# Revit family: 879-000X1X-001-DN65-600
name_source: partatom
category: Pipe Accessories
units: mm (PartAtom-declared; Revit-internal decimal feet)

## family parameters
Always vertical = Yes
Cut with Voids When Loaded = No
Part Type = Valve - Breaks Into
Round Connector Dimension = Use Diameter
Shared = No
Work Plane-Based = No

## types (39) — shared parameters
1 = 1 mm  [stored 0.00328084 ft]
879-0065-00-14400051199 = DN65_PN10/16
879-0065-00-144000511A0 = DN65_PN10/16
879-0080-00-14400051199 = DN80_PN10/16
879-0080-00-144000511A0 = DN80_PN10/16
879-0100-00-14400051199 = DN100_PN10/16
879-0100-00-144000511A0 = DN100_PN10/16
879-0125-00-14400051199 = DN125_PN10/16
879-0125-00-144000511A0 = DN125_PN10/16
879-0150-00-14400051199 = DN150_PN10/16
879-0150-00-144000511A0 = DN150_PN10/16
879-0200-00-04400051199 = DN200_PN10
879-0200-00-044000511A0 = DN200_PN10
879-0200-00-14400051199 = DN200_PN16
879-0200-00-144000511A0 = DN200_PN16
879-0250-00-144000511A0 = DN250_PN10
879-0300-00-04400051199 = DN300_PN10
879-0300-00-044000511A0 = DN300_PN10
879-0300-00-14400051199 = DN300_PN16
879-0300-00-144000511A0 = DN300_PN16
879-0350-00-04400051199 = DN350_PN10
879-0350-00-044000511A0 = DN350_PN10
879-0350-00-14400051199 = DN350_PN16
879-0350-00-144000511A0 = DN350_PN16
879-0400-00-04400051199 = DN400_PN10
879-0400-00-044000511A0 = DN400_PN10
879-0400-00-14400051199 = DN400_PN16
879-0400-00-144000511A0 = DN400_PN16
879-0450-00-04400051199 = DN450_PN10
879-0450-00-044000511A0 = DN450_PN10
879-0450-00-14400051199 = DN450_PN16
879-0450-00-144000511A0 = DN450_PN16
879-0500-00-04400051199 = DN500_PN10
879-0500-00-044000511A0 = DN500_PN10
879-0500-00-14400051199 = DN500_PN16
879-0500-00-144000511A0 = DN500_PN16
879-0600-00-04400051199 = DN600_PN10
879-0600-00-044000511A0 = DN600_PN10
879-0600-00-14400051199 = DN600_PN16
879-0600-00-144000511A0 = DN600_PN16
Body_wall_thickness = 10 mm  [stored 0.0328084 ft]
Description_ = AVK PRESSURE REDUCING/PRESSURE SUSTAINING CONTROL VALVE
Search_Table = 879-000X1X-001-DN65-600
URL product pages = https://www.avkvalves.com

## per-type parameters (varying)
- 879-0065-00-14400051199_DN65_PN10/16: Body_Collar_Dia=30 mm  [stored 0.0984252 ft]; Body_Collar_Dia_2=26 mm; Body_Flange_Dia=83 mm; Body_Flange_Dia_2=91 mm; Body_Height_1=73 mm; Body_Height_2=36 mm  [stored 0.11811 ft]; Body_Height_3=58 mm; Body_Height_4=51 mm; Body_Top_Dia=13 mm; Body_Top_Dia_2=11 mm; Body_With_Dia=58 mm; Body_With_Dia_1=73 mm; Body_With_Dia_2=78 mm; Bolt_support=223 mm; Bolt_support_2=112 mm; Bolt_support_Dia=12 mm  [stored 0.0393701 ft]; Bolt_support_lenght=53 mm; Bolt_support_lenght_2=63 mm; Bottom_profile=16 mm  [stored 0.0524934 ft]; D1=59 mm; D3=93 mm; D3_Ref=236 mm; DN=65 mm; Fillet_Length=6 mm  [stored 0.019685 ft]; Flange_thickness=19 mm  [stored 0.062336 ft]; H3=425 mm; ID=33 mm  [stored 0.108268 ft]; L=290 mm; PG_Dia=33 mm  [stored 0.108268 ft]; PG_Ref=48 mm; PG_depth=8 mm  [stored 0.0262467 ft]; PG_height=230 mm; PG_height_1=214 mm; PG_ref=53 mm; PR_1=39 mm; P_lenght=29 mm; Pilot_Dia_1=18 mm; Pilot_Dia_2=26 mm; Pilot_Dia_3=12 mm  [stored 0.0393701 ft]; Pilot_Dia_4=6 mm  [stored 0.019685 ft]; Pilot_Dia_5=4 mm  [stored 0.0131234 ft]; Pilot_top_1=257 mm; Pilot_top_ref=65 mm; Profile1_Height=117 mm; Profile1_Length=25 mm  [stored 0.082021 ft]; Profile1_Length_2=17 mm; Profile_Dia=6 mm  [stored 0.019685 ft]; Profile_Dia_2=6 mm  [stored 0.019685 ft]; Profile_Dia_3=12 mm  [stored 0.0393701 ft]; Profile_height ref=41 mm  [stored 0.134514 ft]; T_Height=175 mm; T_Height_2=150 mm; T_Height_Ref_1=25 mm  [stored 0.082021 ft]; T_Height_Ref_2=29 mm; Top_Profile=134 mm; Top_Profile_Ref=139 mm; W=305 mm; W_Ref=223 mm; W_Ref_2=287 mm
- 879-0065-00-144000511A0_DN65_PN10/16: Body_Collar_Dia=30 mm  [stored 0.0984252 ft]; Body_Collar_Dia_2=26 mm; Body_Flange_Dia=83 mm; Body_Flange_Dia_2=91 mm; Body_Height_1=73 mm; Body_Height_2=36 mm  [stored 0.11811 ft]; Body_Height_3=73 mm; Body_Height_4=51 mm; Body_Top_Dia=13 mm; Body_Top_Dia_2=11 mm; Body_With_Dia=58 mm; Body_With_Dia_1=73 mm; Body_With_Dia_2=78 mm; Bolt_support=223 mm; Bolt_support_2=112 mm; Bolt_support_Dia=12 mm  [stored 0.0393701 ft]; Bolt_support_lenght=53 mm; Bolt_support_lenght_2=63 mm; Bottom_profile=16 mm  [stored 0.0524934 ft]; D1=59 mm; D3=93 mm; D3_Ref=236 mm; DN=65 mm; Fillet_Length=6 mm  [stored 0.019685 ft]; Flange_thickness=19 mm  [stored 0.062336 ft]; H3=425 mm; ID=33 mm  [stored 0.108268 ft]; L=290 mm; PG_Dia=33 mm  [stored 0.108268 ft]; PG_Ref=48 mm; PG_depth=8 mm  [stored 0.0262467 ft]; PG_height=244 mm; PG_height_1=228 mm; PG_ref=53 mm; PR_1=35 mm  [stored 0.114829 ft]; P_lenght=29 mm; Pilot_Dia_1=18 mm; Pilot_Dia_2=26 mm; Pilot_Dia_3=12 mm  [stored 0.0393701 ft]; Pilot_Dia_4=6 mm  [stored 0.019685 ft]; Pilot_Dia_5=4 mm  [stored 0.0131234 ft]; Pilot_top_1=264 mm; Pilot_top_ref=58 mm; Profile1_Height=135 mm; Profile1_Length=25 mm  [stored 0.082021 ft]; Profile1_Length_2=17 mm; Profile_Dia=6 mm  [stored 0.019685 ft]; Profile_Dia_2=6 mm  [stored 0.019685 ft]; Profile_Dia_3=12 mm  [stored 0.0393701 ft]; Profile_height ref=41 mm  [stored 0.134514 ft]; T_Height=157 mm; T_Height_2=134 mm; T_Height_Ref_1=22 mm  [stored 0.0721785 ft]; T_Height_Ref_2=26 mm; Top_Profile=134 mm; Top_Profile_Ref=139 mm; W=305 mm; W_Ref=223 mm; W_Ref_2=287 mm
- 879-0080-00-14400051199_DN80_PN10/16: Body_Collar_Dia=32 mm; Body_Collar_Dia_2=28 mm  [stored 0.0918635 ft]; Body_Flange_Dia=89 mm; Body_Flange_Dia_2=97 mm; Body_Height_1=78 mm; Body_Height_2=39 mm; Body_Height_3=62 mm; Body_Height_4=54 mm; Body_Top_Dia=14 mm  [stored 0.0459318 ft]; Body_Top_Dia_2=12 mm  [stored 0.0393701 ft]; Body_With_Dia=62 mm; Body_With_Dia_1=78 mm; Body_With_Dia_2=84 mm; Bolt_support=238 mm; Bolt_support_2=119 mm; Bolt_support_Dia=12 mm  [stored 0.0393701 ft]; Bolt_support_lenght=60 mm; Bolt_support_lenght_2=70 mm; Bottom_profile=20 mm  [stored 0.0656168 ft]; D1=66 mm; D3=100 mm; D3_Ref=254 mm; DN=80 mm; Fillet_Length=6 mm  [stored 0.019685 ft]; Flange_thickness=19 mm  [stored 0.062336 ft]; H3=440 mm; ID=40 mm  [stored 0.131234 ft]; L=310 mm; PG_Dia=40 mm  [stored 0.131234 ft]; PG_Ref=52 mm; PG_depth=8 mm  [stored 0.0262467 ft]; PG_height=260 mm; PG_height_1=240 mm; PG_ref=60 mm; PR_1=35 mm  [stored 0.114829 ft]; P_lenght=32 mm; Pilot_Dia_1=20 mm  [stored 0.0656168 ft]; Pilot_Dia_2=29 mm; Pilot_Dia_3=13 mm; Pilot_Dia_4=7 mm  [stored 0.0229659 ft]; Pilot_Dia_5=4 mm  [stored 0.0131234 ft]; Pilot_top_1=267 mm; Pilot_top_ref=63 mm; Profile1_Height=144 mm; Profile1_Length=27 mm; Profile1_Length_2=18 mm; Profile_Dia=6 mm  [stored 0.019685 ft]; Profile_Dia_2=6 mm  [stored 0.019685 ft]; Profile_Dia_3=12 mm  [stored 0.0393701 ft]; Profile_height ref=41 mm  [stored 0.134514 ft]; T_Height=155 mm; T_Height_2=133 mm; T_Height_Ref_1=22 mm  [stored 0.0721785 ft]; T_Height_Ref_2=26 mm; Top_Profile=143 mm; Top_Profile_Ref=148 mm; W=325 mm; W_Ref=239 mm; W_Ref_2=307 mm
- 879-0080-00-144000511A0_DN80_PN10/16: Body_Collar_Dia=32 mm; Body_Collar_Dia_2=28 mm  [stored 0.0918635 ft]; Body_Flange_Dia=89 mm; Body_Flange_Dia_2=97 mm; Body_Height_1=78 mm; Body_Height_2=39 mm; Body_Height_3=78 mm; Body_Height_4=54 mm; Body_Top_Dia=14 mm  [stored 0.0459318 ft]; Body_Top_Dia_2=12 mm  [stored 0.0393701 ft]; Body_With_Dia=62 mm; Body_With_Dia_1=78 mm; Body_With_Dia_2=84 mm; Bolt_support=238 mm; Bolt_support_2=119 mm; Bolt_support_Dia=12 mm  [stored 0.0393701 ft]; Bolt_support_lenght=60 mm; Bolt_support_lenght_2=70 mm; Bottom_profile=20 mm  [stored 0.0656168 ft]; D1=66 mm; D3=100 mm; D3_Ref=254 mm; DN=80 mm; Fillet_Length=6 mm  [stored 0.019685 ft]; Flange_thickness=19 mm  [stored 0.062336 ft]; H3=447 mm; ID=40 mm  [stored 0.131234 ft]; L=310 mm; PG_Dia=40 mm  [stored 0.131234 ft]; PG_Ref=52 mm; PG_depth=8 mm  [stored 0.0262467 ft]; PG_height=253 mm; PG_height_1=233 mm; PG_ref=60 mm; PR_1=39 mm; P_lenght=32 mm; Pilot_Dia_1=20 mm  [stored 0.0656168 ft]; Pilot_Dia_2=29 mm; Pilot_Dia_3=13 mm; Pilot_Dia_4=7 mm  [stored 0.0229659 ft]; Pilot_Dia_5=4 mm  [stored 0.0131234 ft]; Pilot_top_1=278 mm; Pilot_top_ref=59 mm; Profile1_Height=133 mm; Profile1_Length=27 mm; Profile1_Length_2=18 mm; Profile_Dia=6 mm  [stored 0.019685 ft]; Profile_Dia_2=6 mm  [stored 0.019685 ft]; Profile_Dia_3=12 mm  [stored 0.0393701 ft]; Profile_height ref=41 mm  [stored 0.134514 ft]; T_Height=173 mm; T_Height_2=148 mm; T_Height_Ref_1=25 mm  [stored 0.082021 ft]; T_Height_Ref_2=29 mm; Top_Profile=143 mm; Top_Profile_Ref=148 mm; W=325 mm; W_Ref=239 mm; W_Ref_2=307 mm
- 879-0100-00-14400051199_DN100_PN10/16: Body_Collar_Dia=36 mm  [stored 0.11811 ft]; Body_Collar_Dia_2=31 mm  [stored 0.101706 ft]; Body_Flange_Dia=100 mm; Body_Flange_Dia_2=109 mm; Body_Height_1=88 mm; Body_Height_2=44 mm; Body_Height_3=59 mm; Body_Height_4=59 mm; Body_Top_Dia=16 mm  [stored 0.0524934 ft]; Body_Top_Dia_2=13 mm; Body_With_Dia=70 mm; Body_With_Dia_1=88 mm; Body_With_Dia_2=95 mm; Bolt_support=269 mm; Bolt_support_2=135 mm; Bolt_support_Dia=12 mm  [stored 0.0393701 ft]; Bolt_support_lenght=70 mm; Bolt_support_lenght_2=80 mm; Bottom_profile=25 mm  [stored 0.082021 ft]; D1=78 mm; D3=110 mm; D3_Ref=274 mm; DN=100 mm; Fillet_Length=6 mm  [stored 0.019685 ft]; Flange_thickness=19 mm  [stored 0.062336 ft]; H3=460 mm; ID=50 mm; L=350 mm; PG_Dia=50 mm; PG_Ref=58 mm; PG_depth=8 mm  [stored 0.0262467 ft]; PG_height=277 mm; PG_height_1=252 mm; PG_ref=70 mm; PR_1=36 mm  [stored 0.11811 ft]; P_lenght=36 mm  [stored 0.11811 ft]; Pilot_Dia_1=22 mm  [stored 0.0721785 ft]; Pilot_Dia_2=33 mm  [stored 0.108268 ft]; Pilot_Dia_3=15 mm  [stored 0.0492126 ft]; Pilot_Dia_4=7 mm  [stored 0.0229659 ft]; Pilot_Dia_5=5 mm  [stored 0.0164042 ft]; Pilot_top_1=277 mm; Pilot_top_ref=63 mm; Profile1_Height=150 mm; Profile1_Length=30 mm  [stored 0.0984252 ft]; Profile1_Length_2=20 mm  [stored 0.0656168 ft]; Profile_Dia=6 mm  [stored 0.019685 ft]; Profile_Dia_2=6 mm  [stored 0.019685 ft]; Profile_Dia_3=12 mm  [stored 0.0393701 ft]; Profile_height ref=41 mm  [stored 0.134514 ft]; T_Height=159 mm; T_Height_2=136 mm; T_Height_Ref_1=23 mm  [stored 0.0754593 ft]; T_Height_Ref_2=27 mm; Top_Profile=162 mm; Top_Profile_Ref=167 mm; W=345 mm; W_Ref=257 mm; W_Ref_2=327 mm
- 879-0100-00-144000511A0_DN100_PN10/16: Body_Collar_Dia=36 mm  [stored 0.11811 ft]; Body_Collar_Dia_2=31 mm  [stored 0.101706 ft]; Body_Flange_Dia=100 mm; Body_Flange_Dia_2=109 mm; Body_Height_1=88 mm; Body_Height_2=44 mm; Body_Height_3=70 mm; Body_Height_4=59 mm; Body_Top_Dia=16 mm  [stored 0.0524934 ft]; Body_Top_Dia_2=13 mm; Body_With_Dia=70 mm; Body_With_Dia_1=88 mm; Body_With_Dia_2=95 mm; Bolt_support=269 mm; Bolt_support_2=135 mm; Bolt_support_Dia=12 mm  [stored 0.0393701 ft]; Bolt_support_lenght=70 mm; Bolt_support_lenght_2=80 mm; Bottom_profile=25 mm  [stored 0.082021 ft]; D1=78 mm; D3=110 mm; D3_Ref=274 mm; DN=100 mm; Fillet_Length=6 mm  [stored 0.019685 ft]; Flange_thickness=19 mm  [stored 0.062336 ft]; H3=461 mm; ID=50 mm; L=350 mm; PG_Dia=50 mm; PG_Ref=58 mm; PG_depth=8 mm  [stored 0.0262467 ft]; PG_height=270 mm; PG_height_1=245 mm; PG_ref=70 mm; PR_1=38 mm; P_lenght=36 mm  [stored 0.11811 ft]; Pilot_Dia_1=22 mm  [stored 0.0721785 ft]; Pilot_Dia_2=33 mm  [stored 0.108268 ft]; Pilot_Dia_3=15 mm  [stored 0.0492126 ft]; Pilot_Dia_4=7 mm  [stored 0.0229659 ft]; Pilot_Dia_5=5 mm  [stored 0.0164042 ft]; Pilot_top_1=284 mm; Pilot_top_ref=57 mm; Profile1_Height=141 mm; Profile1_Length=30 mm  [stored 0.0984252 ft]; Profile1_Length_2=20 mm  [stored 0.0656168 ft]; Profile_Dia=6 mm  [stored 0.019685 ft]; Profile_Dia_2=6 mm  [stored 0.019685 ft]; Profile_Dia_3=12 mm  [stored 0.0393701 ft]; Profile_height ref=41 mm  [stored 0.134514 ft]; T_Height=169 mm; T_Height_2=145 mm; T_Height_Ref_1=24 mm  [stored 0.0787402 ft]; T_Height_Ref_2=28 mm  [stored 0.0918635 ft]; Top_Profile=162 mm; Top_Profile_Ref=167 mm; W=345 mm; W_Ref=257 mm; W_Ref_2=327 mm
- 879-0125-00-14400051199_DN125_PN10/16: Body_Collar_Dia=42 mm  [stored 0.137795 ft]; Body_Collar_Dia_2=36 mm  [stored 0.11811 ft]; Body_Flange_Dia=114 mm; Body_Flange_Dia_2=125 mm; Body_Height_1=100 mm; Body_Height_2=50 mm; Body_Height_3=65 mm; Body_Height_4=65 mm; Body_Top_Dia=18 mm; Body_Top_Dia_2=15 mm  [stored 0.0492126 ft]; Body_With_Dia=80 mm; Body_With_Dia_1=100 mm; Body_With_Dia_2=108 mm; Bolt_support=308 mm; Bolt_support_2=154 mm; Bolt_support_Dia=12 mm  [stored 0.0393701 ft]; Bolt_support_lenght=83 mm; Bolt_support_lenght_2=93 mm; Bottom_profile=31 mm  [stored 0.101706 ft]; D1=92 mm; D3=125 mm; D3_Ref=291 mm; DN=125 mm; Fillet_Length=6 mm  [stored 0.019685 ft]; Flange_thickness=19 mm  [stored 0.062336 ft]; H3=475 mm; ID=63 mm; L=400 mm; PG_Dia=63 mm; PG_Ref=67 mm; PG_depth=8 mm  [stored 0.0262467 ft]; PG_height=301 mm; PG_height_1=270 mm; PG_ref=83 mm; PR_1=33 mm  [stored 0.108268 ft]; P_lenght=45 mm; Pilot_Dia_1=28 mm  [stored 0.0918635 ft]; Pilot_Dia_2=41 mm  [stored 0.134514 ft]; Pilot_Dia_3=18 mm; Pilot_Dia_4=9 mm  [stored 0.0295276 ft]; Pilot_Dia_5=6 mm  [stored 0.019685 ft]; Pilot_top_1=290 mm; Pilot_top_ref=50 mm; Profile1_Height=165 mm; Profile1_Length=34 mm; Profile1_Length_2=23 mm  [stored 0.0754593 ft]; Profile_Dia=6 mm  [stored 0.019685 ft]; Profile_Dia_2=6 mm  [stored 0.019685 ft]; Profile_Dia_3=12 mm  [stored 0.0393701 ft]; Profile_height ref=41 mm  [stored 0.134514 ft]; T_Height=144 mm; T_Height_2=123 mm; T_Height_Ref_1=21 mm  [stored 0.0688976 ft]; T_Height_Ref_2=24 mm  [stored 0.0787402 ft]; Top_Profile=185 mm; Top_Profile_Ref=190 mm; W=350 mm; W_Ref=270 mm; W_Ref_2=332 mm
- 879-0125-00-144000511A0_DN125_PN10/16: Body_Collar_Dia=42 mm  [stored 0.137795 ft]; Body_Collar_Dia_2=36 mm  [stored 0.11811 ft]; Body_Flange_Dia=114 mm; Body_Flange_Dia_2=125 mm; Body_Height_1=100 mm; Body_Height_2=50 mm; Body_Height_3=65 mm; Body_Height_4=65 mm; Body_Top_Dia=18 mm; Body_Top_Dia_2=15 mm  [stored 0.0492126 ft]; Body_With_Dia=80 mm; Body_With_Dia_1=100 mm; Body_With_Dia_2=108 mm; Bolt_support=308 mm; Bolt_support_2=154 mm; Bolt_support_Dia=12 mm  [stored 0.0393701 ft]; Bolt_support_lenght=83 mm; Bolt_support_lenght_2=93 mm; Bottom_profile=31 mm  [stored 0.101706 ft]; D1=92 mm; D3=125 mm; D3_Ref=291 mm; DN=125 mm; Fillet_Length=6 mm  [stored 0.019685 ft]; Flange_thickness=19 mm  [stored 0.062336 ft]; H3=480 mm; ID=63 mm; L=400 mm; PG_Dia=63 mm; PG_Ref=67 mm; PG_depth=8 mm  [stored 0.0262467 ft]; PG_height=302 mm; PG_height_1=271 mm; PG_ref=83 mm; PR_1=34 mm; P_lenght=45 mm; Pilot_Dia_1=28 mm  [stored 0.0918635 ft]; Pilot_Dia_2=41 mm  [stored 0.134514 ft]; Pilot_Dia_3=18 mm; Pilot_Dia_4=9 mm  [stored 0.0295276 ft]; Pilot_Dia_5=6 mm  [stored 0.019685 ft]; Pilot_top_1=293 mm; Pilot_top_ref=53 mm; Profile1_Height=165 mm; Profile1_Length=34 mm; Profile1_Length_2=23 mm  [stored 0.0754593 ft]; Profile_Dia=6 mm  [stored 0.019685 ft]; Profile_Dia_2=6 mm  [stored 0.019685 ft]; Profile_Dia_3=12 mm  [stored 0.0393701 ft]; Profile_height ref=41 mm  [stored 0.134514 ft]; T_Height=149 mm; T_Height_2=128 mm; T_Height_Ref_1=21 mm  [stored 0.0688976 ft]; T_Height_Ref_2=25 mm  [stored 0.082021 ft]; Top_Profile=185 mm; Top_Profile_Ref=190 mm; W=350 mm; W_Ref=270 mm; W_Ref_2=332 mm
- 879-0150-00-14400051199_DN150_PN10/16: Body_Collar_Dia=50 mm; Body_Collar_Dia_2=43 mm; Body_Flange_Dia=137 mm; Body_Flange_Dia_2=150 mm; Body_Height_1=120 mm; Body_Height_2=60 mm; Body_Height_3=60 mm; Body_Height_4=75 mm; Body_Top_Dia=22 mm  [stored 0.0721785 ft]; Body_Top_Dia_2=18 mm; Body_With_Dia=96 mm; Body_With_Dia_1=120 mm; Body_With_Dia_2=130 mm; Bolt_support=369 mm; Bolt_support_2=185 mm; Bolt_support_Dia=16 mm  [stored 0.0524934 ft]; Bolt_support_lenght=95 mm; Bolt_support_lenght_2=105 mm; Bottom_profile=38 mm; D1=106 mm; D3=143 mm; D3_Ref=308 mm; DN=150 mm; Fillet_Length=8 mm  [stored 0.0262467 ft]; Flange_thickness=19 mm  [stored 0.062336 ft]; H3=520 mm; ID=75 mm; L=480 mm; PG_Dia=50 mm; PG_Ref=80 mm; PG_depth=11 mm; PG_height=320 mm; PG_height_1=295 mm; PG_ref=95 mm; PR_1=32 mm; P_lenght=51 mm; Pilot_Dia_1=31 mm  [stored 0.101706 ft]; Pilot_Dia_2=47 mm; Pilot_Dia_3=21 mm  [stored 0.0688976 ft]; Pilot_Dia_4=10 mm  [stored 0.0328084 ft]; Pilot_Dia_5=7 mm  [stored 0.0229659 ft]; Pilot_top_1=316 mm; Pilot_top_ref=51 mm; Profile1_Height=195 mm; Profile1_Length=39 mm; Profile1_Length_2=26 mm; Profile_Dia=8 mm  [stored 0.0262467 ft]; Profile_Dia_2=8 mm  [stored 0.0262467 ft]; Profile_Dia_3=16 mm  [stored 0.0524934 ft]; Profile_height ref=43 mm; T_Height=140 mm; T_Height_2=120 mm; T_Height_Ref_1=20 mm  [stored 0.0656168 ft]; T_Height_Ref_2=23 mm  [stored 0.0754593 ft]; Top_Profile=222 mm; Top_Profile_Ref=227 mm; W=355 mm; W_Ref=285 mm; W_Ref_2=331 mm
- 879-0150-00-144000511A0_DN150_PN10/16: Body_Collar_Dia=50 mm; Body_Collar_Dia_2=43 mm; Body_Flange_Dia=137 mm; Body_Flange_Dia_2=150 mm; Body_Height_1=120 mm; Body_Height_2=60 mm; Body_Height_3=68 mm; Body_Height_4=75 mm; Body_Top_Dia=22 mm  [stored 0.0721785 ft]; Body_Top_Dia_2=18 mm; Body_With_Dia=96 mm; Body_With_Dia_1=120 mm; Body_With_Dia_2=130 mm; Bolt_support=369 mm; Bolt_support_2=185 mm; Bolt_support_Dia=16 mm  [stored 0.0524934 ft]; Bolt_support_lenght=95 mm; Bolt_support_lenght_2=105 mm; Bottom_profile=38 mm; D1=106 mm; D3=143 mm; D3_Ref=308 mm; DN=150 mm; Fillet_Length=8 mm  [stored 0.0262467 ft]; Flange_thickness=19 mm  [stored 0.062336 ft]; H3=520 mm; ID=75 mm; L=480 mm; PG_Dia=50 mm; PG_Ref=80 mm; PG_depth=11 mm; PG_height=320 mm; PG_height_1=295 mm; PG_ref=95 mm; PR_1=32 mm; P_lenght=51 mm; Pilot_Dia_1=31 mm  [stored 0.101706 ft]; Pilot_Dia_2=47 mm; Pilot_Dia_3=21 mm  [stored 0.0688976 ft]; Pilot_Dia_4=10 mm  [stored 0.0328084 ft]; Pilot_Dia_5=7 mm  [stored 0.0229659 ft]; Pilot_top_1=320 mm; Pilot_top_ref=47 mm; Profile1_Height=195 mm; Profile1_Length=39 mm; Profile1_Length_2=26 mm; Profile_Dia=8 mm  [stored 0.0262467 ft]; Profile_Dia_2=8 mm  [stored 0.0262467 ft]; Profile_Dia_3=16 mm  [stored 0.0524934 ft]; Profile_height ref=43 mm; T_Height=140 mm; T_Height_2=120 mm; T_Height_Ref_1=20 mm  [stored 0.0656168 ft]; T_Height_Ref_2=23 mm  [stored 0.0754593 ft]; Top_Profile=222 mm; Top_Profile_Ref=227 mm; W=355 mm; W_Ref=285 mm; W_Ref_2=331 mm
- 879-0200-00-04400051199_DN200_PN10: Body_Collar_Dia=63 mm; Body_Collar_Dia_2=54 mm; Body_Flange_Dia=171 mm; Body_Flange_Dia_2=188 mm; Body_Height_1=150 mm; Body_Height_2=75 mm; Body_Height_3=75 mm; Body_Height_4=90 mm; Body_Top_Dia=27 mm; Body_Top_Dia_2=22 mm  [stored 0.0721785 ft]; Body_With_Dia=120 mm; Body_With_Dia_1=150 mm; Body_With_Dia_2=162 mm; Bolt_support=462 mm; Bolt_support_2=231 mm; Bolt_support_Dia=20 mm  [stored 0.0656168 ft]; Bolt_support_lenght=120 mm; Bolt_support_lenght_2=130 mm; Bottom_profile=50 mm; D1=133 mm; D3=170 mm; D3_Ref=375 mm; DN=200 mm; Fillet_Length=10 mm  [stored 0.0328084 ft]; Flange_thickness=20 mm  [stored 0.0656168 ft]; H3=610 mm; ID=100 mm; L=600 mm; PG_Dia=67 mm; PG_Ref=100 mm; PG_depth=14 mm  [stored 0.0459318 ft]; PG_height=385 mm; PG_height_1=352 mm; PG_ref=120 mm; PR_1=36 mm  [stored 0.11811 ft]; P_lenght=64 mm; Pilot_Dia_1=39 mm; Pilot_Dia_2=58 mm; Pilot_Dia_3=26 mm; Pilot_Dia_4=13 mm; Pilot_Dia_5=9 mm  [stored 0.0295276 ft]; Pilot_top_1=378 mm; Pilot_top_ref=53 mm; Profile1_Height=238 mm; Profile1_Length=46 mm; Profile1_Length_2=31 mm  [stored 0.101706 ft]; Profile_Dia=10 mm  [stored 0.0328084 ft]; Profile_Dia_2=10 mm  [stored 0.0328084 ft]; Profile_Dia_3=20 mm  [stored 0.0656168 ft]; Profile_height ref=45 mm; T_Height=157 mm; T_Height_2=135 mm; T_Height_Ref_1=22 mm  [stored 0.0721785 ft]; T_Height_Ref_2=26 mm; Top_Profile=277 mm; Top_Profile_Ref=282 mm; W=440 mm; W_Ref=346 mm; W_Ref_2=410 mm
- 879-0200-00-044000511A0_DN200_PN10: Body_Collar_Dia=63 mm; Body_Collar_Dia_2=54 mm; Body_Flange_Dia=171 mm; Body_Flange_Dia_2=188 mm; Body_Height_1=150 mm; Body_Height_2=75 mm; Body_Height_3=100 mm; Body_Height_4=90 mm; Body_Top_Dia=27 mm; Body_Top_Dia_2=22 mm  [stored 0.0721785 ft]; Body_With_Dia=120 mm; Body_With_Dia_1=150 mm; Body_With_Dia_2=162 mm; Bolt_support=462 mm; Bolt_support_2=231 mm; Bolt_support_Dia=20 mm  [stored 0.0656168 ft]; Bolt_support_lenght=120 mm; Bolt_support_lenght_2=130 mm; Bottom_profile=50 mm; D1=133 mm; D3=170 mm; D3_Ref=375 mm; DN=200 mm; Fillet_Length=10 mm  [stored 0.0328084 ft]; Flange_thickness=20 mm  [stored 0.0656168 ft]; H3=688 mm; ID=100 mm; L=600 mm; PG_Dia=67 mm; PG_Ref=100 mm; PG_depth=14 mm  [stored 0.0459318 ft]; PG_height=404 mm; PG_height_1=371 mm; PG_ref=120 mm; PR_1=53 mm; P_lenght=64 mm; Pilot_Dia_1=39 mm; Pilot_Dia_2=58 mm; Pilot_Dia_3=26 mm; Pilot_Dia_4=13 mm; Pilot_Dia_5=9 mm  [stored 0.0295276 ft]; Pilot_top_1=429 mm; Pilot_top_ref=79 mm; Profile1_Height=240 mm; Profile1_Length=46 mm; Profile1_Length_2=31 mm  [stored 0.101706 ft]; Profile_Dia=10 mm  [stored 0.0328084 ft]; Profile_Dia_2=10 mm  [stored 0.0328084 ft]; Profile_Dia_3=20 mm  [stored 0.0656168 ft]; Profile_height ref=45 mm; T_Height=233 mm; T_Height_2=200 mm; T_Height_Ref_1=33 mm  [stored 0.108268 ft]; T_Height_Ref_2=39 mm; Top_Profile=277 mm; Top_Profile_Ref=282 mm; W=440 mm; W_Ref=346 mm; W_Ref_2=410 mm
- 879-0200-00-14400051199_DN200_PN16: Body_Collar_Dia=63 mm; Body_Collar_Dia_2=54 mm; Body_Flange_Dia=171 mm; Body_Flange_Dia_2=188 mm; Body_Height_1=150 mm; Body_Height_2=75 mm; Body_Height_3=75 mm; Body_Height_4=90 mm; Body_Top_Dia=27 mm; Body_Top_Dia_2=22 mm  [stored 0.0721785 ft]; Body_With_Dia=120 mm; Body_With_Dia_1=150 mm; Body_With_Dia_2=162 mm; Bolt_support=462 mm; Bolt_support_2=231 mm; Bolt_support_Dia=20 mm  [stored 0.0656168 ft]; Bolt_support_lenght=120 mm; Bolt_support_lenght_2=130 mm; Bottom_profile=50 mm; D1=133 mm; D3=170 mm; D3_Ref=375 mm; DN=200 mm; Fillet_Length=10 mm  [stored 0.0328084 ft]; Flange_thickness=20 mm  [stored 0.0656168 ft]; H3=610 mm; ID=100 mm; L=600 mm; PG_Dia=67 mm; PG_Ref=100 mm; PG_depth=14 mm  [stored 0.0459318 ft]; PG_height=385 mm; PG_height_1=352 mm; PG_ref=120 mm; PR_1=36 mm  [stored 0.11811 ft]; P_lenght=64 mm; Pilot_Dia_1=39 mm; Pilot_Dia_2=58 mm; Pilot_Dia_3=26 mm; Pilot_Dia_4=13 mm; Pilot_Dia_5=9 mm  [stored 0.0295276 ft]; Pilot_top_1=378 mm; Pilot_top_ref=53 mm; Profile1_Height=238 mm; Profile1_Length=46 mm; Profile1_Length_2=31 mm  [stored 0.101706 ft]; Profile_Dia=10 mm  [stored 0.0328084 ft]; Profile_Dia_2=10 mm  [stored 0.0328084 ft]; Profile_Dia_3=20 mm  [stored 0.0656168 ft]; Profile_height ref=45 mm; T_Height=157 mm; T_Height_2=135 mm; T_Height_Ref_1=22 mm  [stored 0.0721785 ft]; T_Height_Ref_2=26 mm; Top_Profile=277 mm; Top_Profile_Ref=282 mm; W=440 mm; W_Ref=346 mm; W_Ref_2=410 mm
- 879-0200-00-144000511A0_DN200_PN16: Body_Collar_Dia=63 mm; Body_Collar_Dia_2=54 mm; Body_Flange_Dia=171 mm; Body_Flange_Dia_2=188 mm; Body_Height_1=150 mm; Body_Height_2=75 mm; Body_Height_3=86 mm; Body_Height_4=90 mm; Body_Top_Dia=27 mm; Body_Top_Dia_2=22 mm  [stored 0.0721785 ft]; Body_With_Dia=120 mm; Body_With_Dia_1=150 mm; Body_With_Dia_2=162 mm; Bolt_support=462 mm; Bolt_support_2=231 mm; Bolt_support_Dia=20 mm  [stored 0.0656168 ft]; Bolt_support_lenght=120 mm; Bolt_support_lenght_2=130 mm; Bottom_profile=50 mm; D1=133 mm; D3=170 mm; D3_Ref=375 mm; DN=200 mm; Fillet_Length=10 mm  [stored 0.0328084 ft]; Flange_thickness=20 mm  [stored 0.0656168 ft]; H3=688 mm; ID=100 mm; L=600 mm; PG_Dia=67 mm; PG_Ref=100 mm; PG_depth=14 mm  [stored 0.0459318 ft]; PG_height=404 mm; PG_height_1=371 mm; PG_ref=120 mm; PR_1=53 mm; P_lenght=64 mm; Pilot_Dia_1=39 mm; Pilot_Dia_2=58 mm; Pilot_Dia_3=26 mm; Pilot_Dia_4=13 mm; Pilot_Dia_5=9 mm  [stored 0.0295276 ft]; Pilot_top_1=422 mm; Pilot_top_ref=86 mm; Profile1_Height=240 mm; Profile1_Length=46 mm; Profile1_Length_2=31 mm  [stored 0.101706 ft]; Profile_Dia=10 mm  [stored 0.0328084 ft]; Profile_Dia_2=10 mm  [stored 0.0328084 ft]; Profile_Dia_3=20 mm  [stored 0.0656168 ft]; Profile_height ref=45 mm; T_Height=233 mm; T_Height_2=200 mm; T_Height_Ref_1=33 mm  [stored 0.108268 ft]; T_Height_Ref_2=39 mm; Top_Profile=277 mm; Top_Profile_Ref=282 mm; W=440 mm; W_Ref=346 mm; W_Ref_2=410 mm
- 879-0250-00-144000511A0_DN250_PN16: Body_Collar_Dia=76 mm; Body_Collar_Dia_2=65 mm; Body_Flange_Dia=209 mm; Body_Flange_Dia_2=228 mm; Body_Height_1=183 mm; Body_Height_2=91 mm; Body_Height_3=90 mm; Body_Height_4=106 mm; Body_Top_Dia=33 mm  [stored 0.108268 ft]; Body_Top_Dia_2=27 mm; Body_With_Dia=146 mm; Body_With_Dia_1=183 mm; Body_With_Dia_2=197 mm; Bolt_support=562 mm; Bolt_support_2=281 mm; Bolt_support_Dia=20 mm  [stored 0.0656168 ft]; Bolt_support_lenght=145 mm; Bolt_support_lenght_2=155 mm; Bottom_profile=63 mm; D1=160 mm; D3=203 mm; D3_Ref=445 mm; DN=250 mm; Fillet_Length=10 mm  [stored 0.0328084 ft]; Flange_thickness=20 mm  [stored 0.0656168 ft]; H3=806 mm; ID=125 mm; L=730 mm; PG_Dia=83 mm; PG_Ref=122 mm; PG_depth=14 mm  [stored 0.0459318 ft]; PG_height=460 mm; PG_height_1=418 mm; PG_ref=145 mm; PR_1=66 mm; P_lenght=73 mm; Pilot_Dia_1=44 mm; Pilot_Dia_2=66 mm; Pilot_Dia_3=29 mm; Pilot_Dia_4=15 mm  [stored 0.0492126 ft]; Pilot_Dia_5=10 mm  [stored 0.0328084 ft]; Pilot_top_1=491 mm; Pilot_top_ref=102 mm; Profile1_Height=265 mm; Profile1_Length=55 mm; Profile1_Length_2=36 mm  [stored 0.11811 ft]; Profile_Dia=10 mm  [stored 0.0328084 ft]; Profile_Dia_2=10 mm  [stored 0.0328084 ft]; Profile_Dia_3=20 mm  [stored 0.0656168 ft]; Profile_height ref=45 mm; T_Height=294 mm; T_Height_2=252 mm; T_Height_Ref_1=42 mm  [stored 0.137795 ft]; T_Height_Ref_2=49 mm; Top_Profile=337 mm; Top_Profile_Ref=342 mm; W=515 mm; W_Ref=412 mm; W_Ref_2=485 mm
- 879-0300-00-04400051199_DN300_PN10: Body_Collar_Dia=89 mm; Body_Collar_Dia_2=76 mm; Body_Flange_Dia=243 mm; Body_Flange_Dia_2=266 mm; Body_Height_1=213 mm; Body_Height_2=106 mm; Body_Height_3=95 mm; Body_Height_4=121 mm; Body_Top_Dia=38 mm; Body_Top_Dia_2=32 mm; Body_With_Dia=170 mm; Body_With_Dia_1=213 mm; Body_With_Dia_2=230 mm; Bolt_support=654 mm; Bolt_support_2=327 mm; Bolt_support_Dia=20 mm  [stored 0.0656168 ft]; Bolt_support_lenght=170 mm; Bolt_support_lenght_2=180 mm; Bottom_profile=75 mm; D1=185 mm; D3=223 mm; D3_Ref=490 mm; DN=300 mm; Fillet_Length=10 mm  [stored 0.0328084 ft]; Flange_thickness=25 mm  [stored 0.082021 ft]; H3=785 mm; ID=150 mm; L=850 mm; PG_Dia=100 mm; PG_Ref=142 mm; PG_depth=14 mm  [stored 0.0459318 ft]; PG_height=498 mm; PG_height_1=448 mm; PG_ref=170 mm; PR_1=48 mm; P_lenght=87 mm; Pilot_Dia_1=53 mm; Pilot_Dia_2=79 mm; Pilot_Dia_3=35 mm  [stored 0.114829 ft]; Pilot_Dia_4=18 mm; Pilot_Dia_5=12 mm  [stored 0.0393701 ft]; Pilot_top_1=495 mm; Pilot_top_ref=57 mm; Profile1_Height=305 mm; Profile1_Length=60 mm; Profile1_Length_2=40 mm  [stored 0.131234 ft]; Profile_Dia=10 mm  [stored 0.0328084 ft]; Profile_Dia_2=10 mm  [stored 0.0328084 ft]; Profile_Dia_3=20 mm  [stored 0.0656168 ft]; Profile_height ref=45 mm; T_Height=213 mm; T_Height_2=182 mm; T_Height_Ref_1=30 mm  [stored 0.0984252 ft]; T_Height_Ref_2=35 mm  [stored 0.114829 ft]; Top_Profile=392 mm; Top_Profile_Ref=397 mm; W=565 mm; W_Ref=451 mm; W_Ref_2=535 mm
- 879-0300-00-044000511A0_DN300_PN10: Body_Collar_Dia=89 mm; Body_Collar_Dia_2=76 mm; Body_Flange_Dia=243 mm; Body_Flange_Dia_2=266 mm; Body_Height_1=213 mm; Body_Height_2=106 mm; Body_Height_3=106 mm; Body_Height_4=121 mm; Body_Top_Dia=38 mm; Body_Top_Dia_2=32 mm; Body_With_Dia=170 mm; Body_With_Dia_1=213 mm; Body_With_Dia_2=230 mm; Bolt_support=654 mm; Bolt_support_2=327 mm; Bolt_support_Dia=20 mm  [stored 0.0656168 ft]; Bolt_support_lenght=170 mm; Bolt_support_lenght_2=180 mm; Bottom_profile=75 mm; D1=185 mm; D3=223 mm; D3_Ref=490 mm; DN=300 mm; Fillet_Length=10 mm  [stored 0.0328084 ft]; Flange_thickness=25 mm  [stored 0.082021 ft]; H3=881 mm; ID=150 mm; L=850 mm; PG_Dia=100 mm; PG_Ref=142 mm; PG_depth=14 mm  [stored 0.0459318 ft]; PG_height=543 mm; PG_height_1=493 mm; PG_ref=170 mm; PR_1=63 mm; P_lenght=87 mm; Pilot_Dia_1=53 mm; Pilot_Dia_2=79 mm; Pilot_Dia_3=35 mm  [stored 0.114829 ft]; Pilot_Dia_4=18 mm; Pilot_Dia_5=12 mm  [stored 0.0393701 ft]; Pilot_top_1=549 mm; Pilot_top_ref=99 mm; Profile1_Height=335 mm; Profile1_Length=60 mm; Profile1_Length_2=40 mm  [stored 0.131234 ft]; Profile_Dia=10 mm  [stored 0.0328084 ft]; Profile_Dia_2=10 mm  [stored 0.0328084 ft]; Profile_Dia_3=20 mm  [stored 0.0656168 ft]; Profile_height ref=45 mm; T_Height=279 mm; T_Height_2=239 mm; T_Height_Ref_1=40 mm  [stored 0.131234 ft]; T_Height_Ref_2=46 mm; Top_Profile=392 mm; Top_Profile_Ref=397 mm; W=565 mm; W_Ref=451 mm; W_Ref_2=535 mm
- 879-0300-00-14400051199_DN300_PN16: Body_Collar_Dia=89 mm; Body_Collar_Dia_2=76 mm; Body_Flange_Dia=243 mm; Body_Flange_Dia_2=266 mm; Body_Height_1=213 mm; Body_Height_2=106 mm; Body_Height_3=95 mm; Body_Height_4=121 mm; Body_Top_Dia=38 mm; Body_Top_Dia_2=32 mm; Body_With_Dia=170 mm; Body_With_Dia_1=213 mm; Body_With_Dia_2=230 mm; Bolt_support=654 mm; Bolt_support_2=327 mm; Bolt_support_Dia=20 mm  [stored 0.0656168 ft]; Bolt_support_lenght=170 mm; Bolt_support_lenght_2=180 mm; Bottom_profile=75 mm; D1=185 mm; D3=230 mm; D3_Ref=498 mm; DN=300 mm; Fillet_Length=10 mm  [stored 0.0328084 ft]; Flange_thickness=25 mm  [stored 0.082021 ft]; H3=785 mm; ID=150 mm; L=850 mm; PG_Dia=100 mm; PG_Ref=142 mm; PG_depth=14 mm  [stored 0.0459318 ft]; PG_height=496 mm; PG_height_1=446 mm; PG_ref=170 mm; PR_1=46 mm; P_lenght=90 mm; Pilot_Dia_1=55 mm; Pilot_Dia_2=82 mm; Pilot_Dia_3=36 mm  [stored 0.11811 ft]; Pilot_Dia_4=18 mm; Pilot_Dia_5=12 mm  [stored 0.0393701 ft]; Pilot_top_1=492 mm; Pilot_top_ref=53 mm; Profile1_Height=305 mm; Profile1_Length=62 mm; Profile1_Length_2=41 mm  [stored 0.134514 ft]; Profile_Dia=10 mm  [stored 0.0328084 ft]; Profile_Dia_2=10 mm  [stored 0.0328084 ft]; Profile_Dia_3=20 mm  [stored 0.0656168 ft]; Profile_height ref=45 mm; T_Height=205 mm; T_Height_2=176 mm; T_Height_Ref_1=29 mm; T_Height_Ref_2=34 mm; Top_Profile=392 mm; Top_Profile_Ref=397 mm; W=565 mm; W_Ref=457 mm; W_Ref_2=535 mm
- 879-0300-00-144000511A0_DN300_PN16: Body_Collar_Dia=89 mm; Body_Collar_Dia_2=76 mm; Body_Flange_Dia=243 mm; Body_Flange_Dia_2=266 mm; Body_Height_1=213 mm; Body_Height_2=106 mm; Body_Height_3=95 mm; Body_Height_4=121 mm; Body_Top_Dia=38 mm; Body_Top_Dia_2=32 mm; Body_With_Dia=170 mm; Body_With_Dia_1=213 mm; Body_With_Dia_2=230 mm; Bolt_support=654 mm; Bolt_support_2=327 mm; Bolt_support_Dia=20 mm  [stored 0.0656168 ft]; Bolt_support_lenght=170 mm; Bolt_support_lenght_2=180 mm; Bottom_profile=75 mm; D1=185 mm; D3=230 mm; D3_Ref=498 mm; DN=300 mm; Fillet_Length=10 mm  [stored 0.0328084 ft]; Flange_thickness=25 mm  [stored 0.082021 ft]; H3=881 mm; ID=150 mm; L=850 mm; PG_Dia=100 mm; PG_Ref=142 mm; PG_depth=14 mm  [stored 0.0459318 ft]; PG_height=534 mm; PG_height_1=484 mm; PG_ref=170 mm; PR_1=64 mm; P_lenght=90 mm; Pilot_Dia_1=55 mm; Pilot_Dia_2=82 mm; Pilot_Dia_3=36 mm  [stored 0.11811 ft]; Pilot_Dia_4=18 mm; Pilot_Dia_5=12 mm  [stored 0.0393701 ft]; Pilot_top_1=540 mm; Pilot_top_ref=101 mm; Profile1_Height=325 mm; Profile1_Length=62 mm; Profile1_Length_2=41 mm  [stored 0.134514 ft]; Profile_Dia=10 mm  [stored 0.0328084 ft]; Profile_Dia_2=10 mm  [stored 0.0328084 ft]; Profile_Dia_3=20 mm  [stored 0.0656168 ft]; Profile_height ref=45 mm; T_Height=281 mm; T_Height_2=241 mm; T_Height_Ref_1=40 mm  [stored 0.131234 ft]; T_Height_Ref_2=47 mm; Top_Profile=392 mm; Top_Profile_Ref=397 mm; W=565 mm; W_Ref=457 mm; W_Ref_2=535 mm
- 879-0350-00-04400051199_DN350_PN10: Body_Collar_Dia=102 mm; Body_Collar_Dia_2=88 mm; Body_Flange_Dia=280 mm; Body_Flange_Dia_2=306 mm; Body_Height_1=245 mm; Body_Height_2=123 mm; Body_Height_3=98 mm; Body_Height_4=138 mm; Body_Top_Dia=44 mm; Body_Top_Dia_2=37 mm; Body_With_Dia=196 mm; Body_With_Dia_1=245 mm; Body_With_Dia_2=265 mm; Bolt_support=754 mm; Bolt_support_2=377 mm; Bolt_support_Dia=30 mm  [stored 0.0984252 ft]; Bolt_support_lenght=195 mm; Bolt_support_lenght_2=205 mm; Bottom_profile=88 mm; D1=215 mm; D3=253 mm; D3_Ref=538 mm; DN=350 mm; Fillet_Length=15 mm  [stored 0.0492126 ft]; Flange_thickness=27 mm; H3=865 mm; ID=175 mm; L=980 mm; PG_Dia=117 mm; PG_Ref=163 mm; PG_depth=21 mm  [stored 0.0688976 ft]; PG_height=561 mm; PG_height_1=503 mm; PG_ref=195 mm; PR_1=49 mm; P_lenght=100 mm; Pilot_Dia_1=61 mm; Pilot_Dia_2=91 mm; Pilot_Dia_3=40 mm  [stored 0.131234 ft]; Pilot_Dia_4=20 mm  [stored 0.0656168 ft]; Pilot_Dia_5=13 mm; Pilot_top_1=547 mm; Pilot_top_ref=56 mm; Profile1_Height=345 mm; Profile1_Length=68 mm; Profile1_Length_2=45 mm; Profile_Dia=15 mm  [stored 0.0492126 ft]; Profile_Dia_2=15 mm  [stored 0.0492126 ft]; Profile_Dia_3=30 mm  [stored 0.0984252 ft]; Profile_height ref=50 mm; T_Height=218 mm; T_Height_2=186 mm; T_Height_Ref_1=31 mm  [stored 0.101706 ft]; T_Height_Ref_2=36 mm  [stored 0.11811 ft]; Top_Profile=452 mm; Top_Profile_Ref=457 mm; W=615 mm; W_Ref=492 mm; W_Ref_2=570 mm
- 879-0350-00-044000511A0_DN350_PN10: Body_Collar_Dia=102 mm; Body_Collar_Dia_2=88 mm; Body_Flange_Dia=280 mm; Body_Flange_Dia_2=306 mm; Body_Height_1=245 mm; Body_Height_2=123 mm; Body_Height_3=98 mm; Body_Height_4=138 mm; Body_Top_Dia=44 mm; Body_Top_Dia_2=37 mm; Body_With_Dia=196 mm; Body_With_Dia_1=245 mm; Body_With_Dia_2=265 mm; Bolt_support=754 mm; Bolt_support_2=377 mm; Bolt_support_Dia=30 mm  [stored 0.0984252 ft]; Bolt_support_lenght=195 mm; Bolt_support_lenght_2=205 mm; Bottom_profile=88 mm; D1=215 mm; D3=253 mm; D3_Ref=538 mm; DN=350 mm; Fillet_Length=15 mm  [stored 0.0492126 ft]; Flange_thickness=27 mm; H3=959 mm; ID=175 mm; L=980 mm; PG_Dia=117 mm; PG_Ref=163 mm; PG_depth=21 mm  [stored 0.0688976 ft]; PG_height=582 mm; PG_height_1=524 mm; PG_ref=195 mm; PR_1=70 mm; P_lenght=100 mm; Pilot_Dia_1=61 mm; Pilot_Dia_2=91 mm; Pilot_Dia_3=40 mm  [stored 0.131234 ft]; Pilot_Dia_4=20 mm  [stored 0.0656168 ft]; Pilot_Dia_5=13 mm; Pilot_top_1=594 mm; Pilot_top_ref=103 mm; Profile1_Height=345 mm; Profile1_Length=68 mm; Profile1_Length_2=45 mm; Profile_Dia=15 mm  [stored 0.0492126 ft]; Profile_Dia_2=15 mm  [stored 0.0492126 ft]; Profile_Dia_3=30 mm  [stored 0.0984252 ft]; Profile_height ref=50 mm; T_Height=312 mm; T_Height_2=267 mm; T_Height_Ref_1=45 mm; T_Height_Ref_2=52 mm; Top_Profile=452 mm; Top_Profile_Ref=457 mm; W=615 mm; W_Ref=492 mm; W_Ref_2=570 mm
- 879-0350-00-14400051199_DN350_PN16: Body_Collar_Dia=102 mm; Body_Collar_Dia_2=88 mm; Body_Flange_Dia=280 mm; Body_Flange_Dia_2=306 mm; Body_Height_1=245 mm; Body_Height_2=123 mm; Body_Height_3=89 mm; Body_Height_4=138 mm; Body_Top_Dia=44 mm; Body_Top_Dia_2=37 mm; Body_With_Dia=196 mm; Body_With_Dia_1=245 mm; Body_With_Dia_2=265 mm; Bolt_support=754 mm; Bolt_support_2=377 mm; Bolt_support_Dia=30 mm  [stored 0.0984252 ft]; Bolt_support_lenght=195 mm; Bolt_support_lenght_2=205 mm; Bottom_profile=88 mm; D1=215 mm; D3=260 mm; D3_Ref=545 mm; DN=350 mm; Fillet_Length=15 mm  [stored 0.0492126 ft]; Flange_thickness=27 mm; H3=865 mm; ID=175 mm; L=980 mm; PG_Dia=117 mm; PG_Ref=163 mm; PG_depth=21 mm  [stored 0.0688976 ft]; PG_height=559 mm; PG_height_1=501 mm; PG_ref=195 mm; PR_1=48 mm; P_lenght=104 mm; Pilot_Dia_1=63 mm; Pilot_Dia_2=95 mm; Pilot_Dia_3=42 mm  [stored 0.137795 ft]; Pilot_Dia_4=21 mm  [stored 0.0688976 ft]; Pilot_Dia_5=14 mm  [stored 0.0459318 ft]; Pilot_top_1=538 mm; Pilot_top_ref=57 mm; Profile1_Height=345 mm; Profile1_Length=70 mm; Profile1_Length_2=47 mm; Profile_Dia=15 mm  [stored 0.0492126 ft]; Profile_Dia_2=15 mm  [stored 0.0492126 ft]; Profile_Dia_3=30 mm  [stored 0.0984252 ft]; Profile_height ref=50 mm; T_Height=210 mm; T_Height_2=180 mm; T_Height_Ref_1=30 mm  [stored 0.0984252 ft]; T_Height_Ref_2=35 mm  [stored 0.114829 ft]; Top_Profile=452 mm; Top_Profile_Ref=457 mm; W=615 mm; W_Ref=498 mm; W_Ref_2=570 mm
- 879-0350-00-144000511A0_DN350_PN16: Body_Collar_Dia=102 mm; Body_Collar_Dia_2=88 mm; Body_Flange_Dia=280 mm; Body_Flange_Dia_2=306 mm; Body_Height_1=245 mm; Body_Height_2=123 mm; Body_Height_3=89 mm; Body_Height_4=138 mm; Body_Top_Dia=44 mm; Body_Top_Dia_2=37 mm; Body_With_Dia=196 mm; Body_With_Dia_1=245 mm; Body_With_Dia_2=265 mm; Bolt_support=754 mm; Bolt_support_2=377 mm; Bolt_support_Dia=30 mm  [stored 0.0984252 ft]; Bolt_support_lenght=195 mm; Bolt_support_lenght_2=205 mm; Bottom_profile=88 mm; D1=215 mm; D3=260 mm; D3_Ref=545 mm; DN=350 mm; Fillet_Length=15 mm  [stored 0.0492126 ft]; Flange_thickness=27 mm; H3=959 mm; ID=175 mm; L=980 mm; PG_Dia=117 mm; PG_Ref=163 mm; PG_depth=21 mm  [stored 0.0688976 ft]; PG_height=588 mm; PG_height_1=530 mm; PG_ref=195 mm; PR_1=67 mm; P_lenght=104 mm; Pilot_Dia_1=63 mm; Pilot_Dia_2=95 mm; Pilot_Dia_3=42 mm  [stored 0.137795 ft]; Pilot_Dia_4=21 mm  [stored 0.0688976 ft]; Pilot_Dia_5=14 mm  [stored 0.0459318 ft]; Pilot_top_1=585 mm; Pilot_top_ref=104 mm; Profile1_Height=355 mm; Profile1_Length=70 mm; Profile1_Length_2=47 mm; Profile_Dia=15 mm  [stored 0.0492126 ft]; Profile_Dia_2=15 mm  [stored 0.0492126 ft]; Profile_Dia_3=30 mm  [stored 0.0984252 ft]; Profile_height ref=50 mm; T_Height=294 mm; T_Height_2=252 mm; T_Height_Ref_1=42 mm  [stored 0.137795 ft]; T_Height_Ref_2=49 mm; Top_Profile=452 mm; Top_Profile_Ref=457 mm; W=615 mm; W_Ref=498 mm; W_Ref_2=570 mm
- 879-0400-00-04400051199_DN400_PN10: Body_Collar_Dia=115 mm; Body_Collar_Dia_2=99 mm; Body_Flange_Dia=314 mm; Body_Flange_Dia_2=344 mm; Body_Height_1=275 mm; Body_Height_2=138 mm; Body_Height_3=110 mm; Body_Height_4=153 mm; Body_Top_Dia=49 mm; Body_Top_Dia_2=41 mm  [stored 0.134514 ft]; Body_With_Dia=220 mm; Body_With_Dia_1=275 mm; Body_With_Dia_2=297 mm; Bolt_support=846 mm; Bolt_support_2=423 mm; Bolt_support_Dia=40 mm  [stored 0.131234 ft]; Bolt_support_lenght=220 mm; Bolt_support_lenght_2=230 mm; Bottom_profile=100 mm; D1=240 mm; D3=283 mm; D3_Ref=613 mm; DN=400 mm; Fillet_Length=20 mm  [stored 0.0656168 ft]; Flange_thickness=28 mm  [stored 0.0918635 ft]; H3=990 mm; ID=200 mm; L=1100 mm; PG_Dia=133 mm; PG_Ref=183 mm; PG_depth=28 mm  [stored 0.0918635 ft]; PG_height=634 mm; PG_height_1=567 mm; PG_ref=220 mm; PR_1=61 mm; P_lenght=114 mm; Pilot_Dia_1=69 mm; Pilot_Dia_2=104 mm; Pilot_Dia_3=46 mm; Pilot_Dia_4=23 mm  [stored 0.0754593 ft]; Pilot_Dia_5=15 mm  [stored 0.0492126 ft]; Pilot_top_1=623 mm; Pilot_top_ref=75 mm; Profile1_Height=385 mm; Profile1_Length=76 mm; Profile1_Length_2=51 mm; Profile_Dia=20 mm  [stored 0.0656168 ft]; Profile_Dia_2=20 mm  [stored 0.0656168 ft]; Profile_Dia_3=40 mm  [stored 0.131234 ft]; Profile_height ref=55 mm; T_Height=268 mm; T_Height_2=229 mm; T_Height_Ref_1=38 mm; T_Height_Ref_2=45 mm; Top_Profile=508 mm; Top_Profile_Ref=513 mm; W=720 mm; W_Ref=561 mm; W_Ref_2=660 mm
- 879-0400-00-044000511A0_DN400_PN10: Body_Collar_Dia=115 mm; Body_Collar_Dia_2=99 mm; Body_Flange_Dia=314 mm; Body_Flange_Dia_2=344 mm; Body_Height_1=275 mm; Body_Height_2=138 mm; Body_Height_3=122 mm; Body_Height_4=153 mm; Body_Top_Dia=49 mm; Body_Top_Dia_2=41 mm  [stored 0.134514 ft]; Body_With_Dia=220 mm; Body_With_Dia_1=275 mm; Body_With_Dia_2=297 mm; Bolt_support=846 mm; Bolt_support_2=423 mm; Bolt_support_Dia=40 mm  [stored 0.131234 ft]; Bolt_support_lenght=220 mm; Bolt_support_lenght_2=230 mm; Bottom_profile=100 mm; D1=240 mm; D3=283 mm; D3_Ref=613 mm; DN=400 mm; Fillet_Length=20 mm  [stored 0.0656168 ft]; Flange_thickness=28 mm  [stored 0.0918635 ft]; H3=1159 mm; ID=200 mm; L=1100 mm; PG_Dia=133 mm; PG_Ref=183 mm; PG_depth=28 mm  [stored 0.0918635 ft]; PG_height=680 mm; PG_height_1=613 mm; PG_ref=220 mm; PR_1=96 mm; P_lenght=114 mm; Pilot_Dia_1=69 mm; Pilot_Dia_2=104 mm; Pilot_Dia_3=46 mm; Pilot_Dia_4=23 mm  [stored 0.0754593 ft]; Pilot_Dia_5=15 mm  [stored 0.0492126 ft]; Pilot_top_1=713 mm; Pilot_top_ref=154 mm; Profile1_Height=395 mm; Profile1_Length=76 mm; Profile1_Length_2=51 mm; Profile_Dia=20 mm  [stored 0.0656168 ft]; Profile_Dia_2=20 mm  [stored 0.0656168 ft]; Profile_Dia_3=40 mm  [stored 0.131234 ft]; Profile_height ref=55 mm; T_Height=427 mm; T_Height_2=366 mm; T_Height_Ref_1=61 mm; T_Height_Ref_2=71 mm; Top_Profile=508 mm; Top_Profile_Ref=513 mm; W=720 mm; W_Ref=561 mm; W_Ref_2=660 mm
- 879-0400-00-14400051199_DN400_PN16: Body_Collar_Dia=115 mm; Body_Collar_Dia_2=99 mm; Body_Flange_Dia=314 mm; Body_Flange_Dia_2=344 mm; Body_Height_1=275 mm; Body_Height_2=138 mm; Body_Height_3=100 mm; Body_Height_4=153 mm; Body_Top_Dia=49 mm; Body_Top_Dia_2=41 mm  [stored 0.134514 ft]; Body_With_Dia=220 mm; Body_With_Dia_1=275 mm; Body_With_Dia_2=297 mm; Bolt_support=846 mm; Bolt_support_2=423 mm; Bolt_support_Dia=40 mm  [stored 0.131234 ft]; Bolt_support_lenght=220 mm; Bolt_support_lenght_2=230 mm; Bottom_profile=100 mm; D1=240 mm; D3=290 mm; D3_Ref=620 mm; DN=400 mm; Fillet_Length=20 mm  [stored 0.0656168 ft]; Flange_thickness=28 mm  [stored 0.0918635 ft]; H3=990 mm; ID=200 mm; L=1100 mm; PG_Dia=133 mm; PG_Ref=183 mm; PG_depth=28 mm  [stored 0.0918635 ft]; PG_height=632 mm; PG_height_1=566 mm; PG_ref=220 mm; PR_1=59 mm; P_lenght=117 mm; Pilot_Dia_1=71 mm; Pilot_Dia_2=107 mm; Pilot_Dia_3=47 mm; Pilot_Dia_4=24 mm  [stored 0.0787402 ft]; Pilot_Dia_5=16 mm  [stored 0.0524934 ft]; Pilot_top_1=614 mm; Pilot_top_ref=76 mm; Profile1_Height=385 mm; Profile1_Length=78 mm; Profile1_Length_2=52 mm; Profile_Dia=20 mm  [stored 0.0656168 ft]; Profile_Dia_2=20 mm  [stored 0.0656168 ft]; Profile_Dia_3=40 mm  [stored 0.131234 ft]; Profile_height ref=55 mm; T_Height=260 mm; T_Height_2=223 mm; T_Height_Ref_1=37 mm; T_Height_Ref_2=43 mm; Top_Profile=508 mm; Top_Profile_Ref=513 mm; W=720 mm; W_Ref=567 mm; W_Ref_2=660 mm
- 879-0400-00-144000511A0_DN400_PN16: Body_Collar_Dia=115 mm; Body_Collar_Dia_2=99 mm; Body_Flange_Dia=314 mm; Body_Flange_Dia_2=344 mm; Body_Height_1=275 mm; Body_Height_2=138 mm; Body_Height_3=110 mm; Body_Height_4=153 mm; Body_Top_Dia=49 mm; Body_Top_Dia_2=41 mm  [stored 0.134514 ft]; Body_With_Dia=220 mm; Body_With_Dia_1=275 mm; Body_With_Dia_2=297 mm; Bolt_support=846 mm; Bolt_support_2=423 mm; Bolt_support_Dia=40 mm  [stored 0.131234 ft]; Bolt_support_lenght=220 mm; Bolt_support_lenght_2=230 mm; Bottom_profile=100 mm; D1=240 mm; D3=290 mm; D3_Ref=620 mm; DN=400 mm; Fillet_Length=20 mm  [stored 0.0656168 ft]; Flange_thickness=28 mm  [stored 0.0918635 ft]; H3=1159 mm; ID=200 mm; L=1100 mm; PG_Dia=133 mm; PG_Ref=183 mm; PG_depth=28 mm  [stored 0.0918635 ft]; PG_height=686 mm; PG_height_1=619 mm; PG_ref=220 mm; PR_1=93 mm; P_lenght=117 mm; Pilot_Dia_1=71 mm; Pilot_Dia_2=107 mm; Pilot_Dia_3=47 mm; Pilot_Dia_4=24 mm  [stored 0.0787402 ft]; Pilot_Dia_5=16 mm  [stored 0.0524934 ft]; Pilot_top_1=703 mm; Pilot_top_ref=156 mm; Profile1_Height=405 mm; Profile1_Length=78 mm; Profile1_Length_2=52 mm; Profile_Dia=20 mm  [stored 0.0656168 ft]; Profile_Dia_2=20 mm  [stored 0.0656168 ft]; Profile_Dia_3=40 mm  [stored 0.131234 ft]; Profile_height ref=55 mm; T_Height=409 mm; T_Height_2=351 mm; T_Height_Ref_1=58 mm; T_Height_Ref_2=68 mm; Top_Profile=508 mm; Top_Profile_Ref=513 mm; W=720 mm; W_Ref=567 mm; W_Ref_2=660 mm
- 879-0450-00-04400051199_DN450_PN10: Body_Collar_Dia=125 mm; Body_Collar_Dia_2=108 mm; Body_Flange_Dia=343 mm; Body_Flange_Dia_2=375 mm; Body_Height_1=300 mm; Body_Height_2=150 mm; Body_Height_3=120 mm; Body_Height_4=165 mm; Body_Top_Dia=54 mm; Body_Top_Dia_2=45 mm; Body_With_Dia=240 mm; Body_With_Dia_1=300 mm; Body_With_Dia_2=324 mm; Bolt_support=923 mm; Bolt_support_2=462 mm; Bolt_support_Dia=40 mm  [stored 0.131234 ft]; Bolt_support_lenght=245 mm; Bolt_support_lenght_2=255 mm; Bottom_profile=113 mm; D1=265 mm; D3=308 mm; D3_Ref=673 mm; DN=450 mm; Fillet_Length=20 mm  [stored 0.0656168 ft]; Flange_thickness=30 mm  [stored 0.0984252 ft]; H3=1050 mm; ID=225 mm; L=1200 mm; PG_Dia=150 mm; PG_Ref=200 mm; PG_depth=28 mm  [stored 0.0918635 ft]; PG_height=705 mm; PG_height_1=630 mm; PG_ref=245 mm; PR_1=55 mm; P_lenght=125 mm; Pilot_Dia_1=76 mm; Pilot_Dia_2=113 mm; Pilot_Dia_3=50 mm; Pilot_Dia_4=25 mm  [stored 0.082021 ft]; Pilot_Dia_5=17 mm; Pilot_top_1=664 mm; Pilot_top_ref=69 mm; Profile1_Height=445 mm; Profile1_Length=83 mm; Profile1_Length_2=55 mm; Profile_Dia=20 mm  [stored 0.0656168 ft]; Profile_Dia_2=20 mm  [stored 0.0656168 ft]; Profile_Dia_3=40 mm  [stored 0.131234 ft]; Profile_height ref=55 mm; T_Height=243 mm; T_Height_2=208 mm; T_Height_Ref_1=35 mm  [stored 0.114829 ft]; T_Height_Ref_2=40 mm  [stored 0.131234 ft]; Top_Profile=554 mm; Top_Profile_Ref=559 mm; W=790 mm; W_Ref=616 mm; W_Ref_2=730 mm
- 879-0450-00-044000511A0_DN450_PN10: Body_Collar_Dia=125 mm; Body_Collar_Dia_2=108 mm; Body_Flange_Dia=343 mm; Body_Flange_Dia_2=375 mm; Body_Height_1=300 mm; Body_Height_2=150 mm; Body_Height_3=120 mm; Body_Height_4=165 mm; Body_Top_Dia=54 mm; Body_Top_Dia_2=45 mm; Body_With_Dia=240 mm; Body_With_Dia_1=300 mm; Body_With_Dia_2=324 mm; Bolt_support=923 mm; Bolt_support_2=462 mm; Bolt_support_Dia=40 mm  [stored 0.131234 ft]; Bolt_support_lenght=245 mm; Bolt_support_lenght_2=255 mm; Bottom_profile=113 mm; D1=265 mm; D3=308 mm; D3_Ref=673 mm; DN=450 mm; Fillet_Length=20 mm  [stored 0.0656168 ft]; Flange_thickness=30 mm  [stored 0.0984252 ft]; H3=1220 mm; ID=225 mm; L=1200 mm; PG_Dia=150 mm; PG_Ref=200 mm; PG_depth=28 mm  [stored 0.0918635 ft]; PG_height=743 mm; PG_height_1=668 mm; PG_ref=245 mm; PR_1=93 mm; P_lenght=125 mm; Pilot_Dia_1=76 mm; Pilot_Dia_2=113 mm; Pilot_Dia_3=50 mm; Pilot_Dia_4=25 mm  [stored 0.082021 ft]; Pilot_Dia_5=17 mm; Pilot_top_1=749 mm; Pilot_top_ref=154 mm; Profile1_Height=445 mm; Profile1_Length=83 mm; Profile1_Length_2=55 mm; Profile_Dia=20 mm  [stored 0.0656168 ft]; Profile_Dia_2=20 mm  [stored 0.0656168 ft]; Profile_Dia_3=40 mm  [stored 0.131234 ft]; Profile_height ref=55 mm; T_Height=413 mm; T_Height_2=354 mm; T_Height_Ref_1=59 mm; T_Height_Ref_2=69 mm; Top_Profile=554 mm; Top_Profile_Ref=559 mm; W=790 mm; W_Ref=616 mm; W_Ref_2=730 mm
- 879-0450-00-14400051199_DN450_PN16: Body_Collar_Dia=125 mm; Body_Collar_Dia_2=108 mm; Body_Flange_Dia=343 mm; Body_Flange_Dia_2=375 mm; Body_Height_1=300 mm; Body_Height_2=150 mm; Body_Height_3=120 mm; Body_Height_4=165 mm; Body_Top_Dia=54 mm; Body_Top_Dia_2=45 mm; Body_With_Dia=240 mm; Body_With_Dia_1=300 mm; Body_With_Dia_2=324 mm; Bolt_support=923 mm; Bolt_support_2=462 mm; Bolt_support_Dia=40 mm  [stored 0.131234 ft]; Bolt_support_lenght=245 mm; Bolt_support_lenght_2=255 mm; Bottom_profile=113 mm; D1=274 mm; D3=320 mm; D3_Ref=685 mm; DN=450 mm; Fillet_Length=20 mm  [stored 0.0656168 ft]; Flange_thickness=30 mm  [stored 0.0984252 ft]; H3=1050 mm; ID=225 mm; L=1200 mm; PG_Dia=150 mm; PG_Ref=200 mm; PG_depth=28 mm  [stored 0.0918635 ft]; PG_height=702 mm; PG_height_1=627 mm; PG_ref=245 mm; PR_1=52 mm; P_lenght=130 mm; Pilot_Dia_1=79 mm; Pilot_Dia_2=119 mm; Pilot_Dia_3=53 mm; Pilot_Dia_4=26 mm; Pilot_Dia_5=18 mm; Pilot_top_1=658 mm; Pilot_top_ref=63 mm; Profile1_Height=445 mm; Profile1_Length=86 mm; Profile1_Length_2=58 mm; Profile_Dia=20 mm  [stored 0.0656168 ft]; Profile_Dia_2=20 mm  [stored 0.0656168 ft]; Profile_Dia_3=40 mm  [stored 0.131234 ft]; Profile_height ref=55 mm; T_Height=230 mm; T_Height_2=197 mm; T_Height_Ref_1=33 mm  [stored 0.108268 ft]; T_Height_Ref_2=38 mm; Top_Profile=554 mm; Top_Profile_Ref=559 mm; W=790 mm; W_Ref=626 mm; W_Ref_2=730 mm
- 879-0450-00-144000511A0_DN450_PN16: Body_Collar_Dia=125 mm; Body_Collar_Dia_2=108 mm; Body_Flange_Dia=343 mm; Body_Flange_Dia_2=375 mm; Body_Height_1=300 mm; Body_Height_2=150 mm; Body_Height_3=120 mm; Body_Height_4=165 mm; Body_Top_Dia=54 mm; Body_Top_Dia_2=45 mm; Body_With_Dia=240 mm; Body_With_Dia_1=300 mm; Body_With_Dia_2=324 mm; Bolt_support=923 mm; Bolt_support_2=462 mm; Bolt_support_Dia=40 mm  [stored 0.131234 ft]; Bolt_support_lenght=245 mm; Bolt_support_lenght_2=255 mm; Bottom_profile=113 mm; D1=274 mm; D3=320 mm; D3_Ref=685 mm; DN=450 mm; Fillet_Length=20 mm  [stored 0.0656168 ft]; Flange_thickness=30 mm  [stored 0.0984252 ft]; H3=1220 mm; ID=225 mm; L=1200 mm; PG_Dia=150 mm; PG_Ref=200 mm; PG_depth=28 mm  [stored 0.0918635 ft]; PG_height=741 mm; PG_height_1=666 mm; PG_ref=245 mm; PR_1=90 mm; P_lenght=130 mm; Pilot_Dia_1=79 mm; Pilot_Dia_2=119 mm; Pilot_Dia_3=53 mm; Pilot_Dia_4=26 mm; Pilot_Dia_5=18 mm; Pilot_top_1=743 mm; Pilot_top_ref=148 mm; Profile1_Height=445 mm; Profile1_Length=86 mm; Profile1_Length_2=58 mm; Profile_Dia=20 mm  [stored 0.0656168 ft]; Profile_Dia_2=20 mm  [stored 0.0656168 ft]; Profile_Dia_3=40 mm  [stored 0.131234 ft]; Profile_height ref=55 mm; T_Height=400 mm; T_Height_2=343 mm; T_Height_Ref_1=57 mm; T_Height_Ref_2=67 mm; Top_Profile=554 mm; Top_Profile_Ref=559 mm; W=790 mm; W_Ref=626 mm; W_Ref_2=730 mm
- 879-0500-00-04400051199_DN500_PN10: Body_Collar_Dia=130 mm; Body_Collar_Dia_2=112 mm; Body_Flange_Dia=357 mm; Body_Flange_Dia_2=391 mm; Body_Height_1=313 mm; Body_Height_2=156 mm; Body_Height_3=125 mm; Body_Height_4=171 mm; Body_Top_Dia=56 mm; Body_Top_Dia_2=47 mm; Body_With_Dia=250 mm; Body_With_Dia_1=313 mm; Body_With_Dia_2=338 mm; Bolt_support=962 mm; Bolt_support_2=481 mm; Bolt_support_Dia=50 mm; Bolt_support_lenght=270 mm; Bolt_support_lenght_2=280 mm; Bottom_profile=125 mm; D1=291 mm; D3=335 mm; D3_Ref=768 mm; DN=500 mm; Fillet_Length=25 mm  [stored 0.082021 ft]; Flange_thickness=32 mm; H3=1235 mm; ID=250 mm; L=1250 mm; PG_Dia=167 mm; PG_Ref=208 mm; PG_depth=35 mm  [stored 0.114829 ft]; PG_height=765 mm; PG_height_1=682 mm; PG_ref=270 mm; PR_1=88 mm; P_lenght=137 mm; Pilot_Dia_1=83 mm; Pilot_Dia_2=125 mm; Pilot_Dia_3=55 mm; Pilot_Dia_4=28 mm  [stored 0.0918635 ft]; Pilot_Dia_5=18 mm; Pilot_top_1=754 mm; Pilot_top_ref=136 mm; Profile1_Height=450 mm; Profile1_Length=91 mm; Profile1_Length_2=60 mm; Profile_Dia=25 mm  [stored 0.082021 ft]; Profile_Dia_2=25 mm  [stored 0.082021 ft]; Profile_Dia_3=50 mm; Profile_height ref=60 mm; T_Height=390 mm; T_Height_2=334 mm; T_Height_Ref_1=56 mm; T_Height_Ref_2=65 mm; Top_Profile=577 mm; Top_Profile_Ref=582 mm; W=940 mm; W_Ref=705 mm; W_Ref_2=865 mm
- 879-0500-00-044000511A0_DN500_PN10: Body_Collar_Dia=130 mm; Body_Collar_Dia_2=112 mm; Body_Flange_Dia=357 mm; Body_Flange_Dia_2=391 mm; Body_Height_1=313 mm; Body_Height_2=156 mm; Body_Height_3=125 mm; Body_Height_4=171 mm; Body_Top_Dia=56 mm; Body_Top_Dia_2=47 mm; Body_With_Dia=250 mm; Body_With_Dia_1=313 mm; Body_With_Dia_2=338 mm; Bolt_support=962 mm; Bolt_support_2=481 mm; Bolt_support_Dia=50 mm; Bolt_support_lenght=270 mm; Bolt_support_lenght_2=280 mm; Bottom_profile=125 mm; D1=291 mm; D3=335 mm; D3_Ref=768 mm; DN=500 mm; Fillet_Length=25 mm  [stored 0.082021 ft]; Flange_thickness=32 mm; H3=1408 mm; ID=250 mm; L=1250 mm; PG_Dia=167 mm; PG_Ref=208 mm; PG_depth=35 mm  [stored 0.114829 ft]; PG_height=816 mm; PG_height_1=732 mm; PG_ref=270 mm; PR_1=124 mm; P_lenght=137 mm; Pilot_Dia_1=83 mm; Pilot_Dia_2=125 mm; Pilot_Dia_3=55 mm; Pilot_Dia_4=28 mm  [stored 0.0918635 ft]; Pilot_Dia_5=18 mm; Pilot_top_1=841 mm; Pilot_top_ref=222 mm; Profile1_Height=465 mm; Profile1_Length=91 mm; Profile1_Length_2=60 mm; Profile_Dia=25 mm  [stored 0.082021 ft]; Profile_Dia_2=25 mm  [stored 0.082021 ft]; Profile_Dia_3=50 mm; Profile_height ref=60 mm; T_Height=548 mm; T_Height_2=470 mm; T_Height_Ref_1=78 mm; T_Height_Ref_2=91 mm; Top_Profile=577 mm; Top_Profile_Ref=582 mm; W=940 mm; W_Ref=705 mm; W_Ref_2=865 mm
- 879-0500-00-14400051199_DN500_PN16: Body_Collar_Dia=130 mm; Body_Collar_Dia_2=112 mm; Body_Flange_Dia=357 mm; Body_Flange_Dia_2=391 mm; Body_Height_1=313 mm; Body_Height_2=156 mm; Body_Height_3=125 mm; Body_Height_4=171 mm; Body_Top_Dia=56 mm; Body_Top_Dia_2=47 mm; Body_With_Dia=250 mm; Body_With_Dia_1=313 mm; Body_With_Dia_2=338 mm; Bolt_support=962 mm; Bolt_support_2=481 mm; Bolt_support_Dia=50 mm; Bolt_support_lenght=270 mm; Bolt_support_lenght_2=280 mm; Bottom_profile=125 mm; D1=305 mm; D3=358 mm; D3_Ref=790 mm; DN=500 mm; Fillet_Length=25 mm  [stored 0.082021 ft]; Flange_thickness=32 mm; H3=1235 mm; ID=250 mm; L=1250 mm; PG_Dia=167 mm; PG_Ref=208 mm; PG_depth=35 mm  [stored 0.114829 ft]; PG_height=764 mm; PG_height_1=680 mm; PG_ref=270 mm; PR_1=82 mm; P_lenght=147 mm; Pilot_Dia_1=89 mm; Pilot_Dia_2=134 mm; Pilot_Dia_3=59 mm; Pilot_Dia_4=30 mm  [stored 0.0984252 ft]; Pilot_Dia_5=20 mm  [stored 0.0656168 ft]; Pilot_top_1=743 mm; Pilot_top_ref=124 mm; Profile1_Height=455 mm; Profile1_Length=97 mm; Profile1_Length_2=64 mm; Profile_Dia=25 mm  [stored 0.082021 ft]; Profile_Dia_2=25 mm  [stored 0.082021 ft]; Profile_Dia_3=50 mm; Profile_height ref=60 mm; T_Height=363 mm; T_Height_2=311 mm; T_Height_Ref_1=52 mm; T_Height_Ref_2=60 mm; Top_Profile=577 mm; Top_Profile_Ref=582 mm; W=940 mm; W_Ref=723 mm; W_Ref_2=865 mm
- 879-0500-00-144000511A0_DN500_PN16: Body_Collar_Dia=130 mm; Body_Collar_Dia_2=112 mm; Body_Flange_Dia=357 mm; Body_Flange_Dia_2=391 mm; Body_Height_1=313 mm; Body_Height_2=156 mm; Body_Height_3=125 mm; Body_Height_4=171 mm; Body_Top_Dia=56 mm; Body_Top_Dia_2=47 mm; Body_With_Dia=250 mm; Body_With_Dia_1=313 mm; Body_With_Dia_2=338 mm; Bolt_support=962 mm; Bolt_support_2=481 mm; Bolt_support_Dia=50 mm; Bolt_support_lenght=270 mm; Bolt_support_lenght_2=280 mm; Bottom_profile=125 mm; D1=305 mm; D3=358 mm; D3_Ref=790 mm; DN=500 mm; Fillet_Length=25 mm  [stored 0.082021 ft]; Flange_thickness=32 mm; H3=1408 mm; ID=250 mm; L=1250 mm; PG_Dia=167 mm; PG_Ref=208 mm; PG_depth=35 mm  [stored 0.114829 ft]; PG_height=803 mm; PG_height_1=720 mm; PG_ref=270 mm; PR_1=121 mm; P_lenght=147 mm; Pilot_Dia_1=89 mm; Pilot_Dia_2=134 mm; Pilot_Dia_3=59 mm; Pilot_Dia_4=30 mm  [stored 0.0984252 ft]; Pilot_Dia_5=20 mm  [stored 0.0656168 ft]; Pilot_top_1=830 mm; Pilot_top_ref=211 mm; Profile1_Height=455 mm; Profile1_Length=97 mm; Profile1_Length_2=64 mm; Profile_Dia=25 mm  [stored 0.082021 ft]; Profile_Dia_2=25 mm  [stored 0.082021 ft]; Profile_Dia_3=50 mm; Profile_height ref=60 mm; T_Height=536 mm; T_Height_2=459 mm; T_Height_Ref_1=77 mm; T_Height_Ref_2=89 mm; Top_Profile=577 mm; Top_Profile_Ref=582 mm; W=940 mm; W_Ref=723 mm; W_Ref_2=865 mm
- 879-0600-00-04400051199_DN600_PN10: Body_Collar_Dia=151 mm; Body_Collar_Dia_2=130 mm; Body_Flange_Dia=414 mm; Body_Flange_Dia_2=453 mm; Body_Height_1=363 mm; Body_Height_2=181 mm; Body_Height_3=145 mm; Body_Height_4=196 mm; Body_Top_Dia=65 mm; Body_Top_Dia_2=54 mm; Body_With_Dia=290 mm; Body_With_Dia_1=363 mm; Body_With_Dia_2=392 mm; Bolt_support=1115 mm; Bolt_support_2=558 mm; Bolt_support_Dia=60 mm; Bolt_support_lenght=320 mm; Bolt_support_lenght_2=330 mm; Bottom_profile=150 mm; D1=341 mm; D3=390 mm; D3_Ref=860 mm; DN=600 mm; Fillet_Length=30 mm  [stored 0.0984252 ft]; Flange_thickness=36 mm  [stored 0.11811 ft]; H3=1345 mm; ID=300 mm; L=1450 mm; PG_Dia=200 mm; PG_Ref=242 mm; PG_depth=42 mm  [stored 0.137795 ft]; PG_height=873 mm; PG_height_1=773 mm; PG_ref=320 mm; PR_1=83 mm; P_lenght=162 mm; Pilot_Dia_1=98 mm; Pilot_Dia_2=147 mm; Pilot_Dia_3=65 mm; Pilot_Dia_4=33 mm  [stored 0.108268 ft]; Pilot_Dia_5=22 mm  [stored 0.0721785 ft]; Pilot_top_1=829 mm; Pilot_top_ref=116 mm; Profile1_Height=525 mm; Profile1_Length=105 mm; Profile1_Length_2=70 mm; Profile_Dia=30 mm  [stored 0.0984252 ft]; Profile_Dia_2=30 mm  [stored 0.0984252 ft]; Profile_Dia_3=60 mm; Profile_height ref=65 mm; T_Height=365 mm; T_Height_2=313 mm; T_Height_Ref_1=52 mm; T_Height_Ref_2=61 mm; Top_Profile=669 mm; Top_Profile_Ref=674 mm; W=1030 mm; W_Ref=787 mm; W_Ref_2=940 mm
- 879-0600-00-044000511A0_DN600_PN10: Body_Collar_Dia=151 mm; Body_Collar_Dia_2=130 mm; Body_Flange_Dia=414 mm; Body_Flange_Dia_2=453 mm; Body_Height_1=363 mm; Body_Height_2=181 mm; Body_Height_3=145 mm; Body_Height_4=196 mm; Body_Top_Dia=65 mm; Body_Top_Dia_2=54 mm; Body_With_Dia=290 mm; Body_With_Dia_1=363 mm; Body_With_Dia_2=392 mm; Bolt_support=1115 mm; Bolt_support_2=558 mm; Bolt_support_Dia=60 mm; Bolt_support_lenght=320 mm; Bolt_support_lenght_2=330 mm; Bottom_profile=150 mm; D1=341 mm; D3=390 mm; D3_Ref=860 mm; DN=600 mm; Fillet_Length=30 mm  [stored 0.0984252 ft]; Flange_thickness=36 mm  [stored 0.11811 ft]; H3=1518 mm; ID=300 mm; L=1450 mm; PG_Dia=200 mm; PG_Ref=242 mm; PG_depth=42 mm  [stored 0.137795 ft]; PG_height=919 mm; PG_height_1=819 mm; PG_ref=320 mm; PR_1=119 mm; P_lenght=162 mm; Pilot_Dia_1=98 mm; Pilot_Dia_2=147 mm; Pilot_Dia_3=65 mm; Pilot_Dia_4=33 mm  [stored 0.108268 ft]; Pilot_Dia_5=22 mm  [stored 0.0721785 ft]; Pilot_top_1=916 mm; Pilot_top_ref=202 mm; Profile1_Height=535 mm; Profile1_Length=105 mm; Profile1_Length_2=70 mm; Profile_Dia=30 mm  [stored 0.0984252 ft]; Profile_Dia_2=30 mm  [stored 0.0984252 ft]; Profile_Dia_3=60 mm; Profile_height ref=65 mm; T_Height=528 mm; T_Height_2=453 mm; T_Height_Ref_1=75 mm; T_Height_Ref_2=88 mm; Top_Profile=669 mm; Top_Profile_Ref=674 mm; W=1030 mm; W_Ref=787 mm; W_Ref_2=940 mm
- 879-0600-00-14400051199_DN600_PN16: Body_Collar_Dia=151 mm; Body_Collar_Dia_2=130 mm; Body_Flange_Dia=414 mm; Body_Flange_Dia_2=453 mm; Body_Height_1=363 mm; Body_Height_2=181 mm; Body_Height_3=145 mm; Body_Height_4=196 mm; Body_Top_Dia=65 mm; Body_Top_Dia_2=54 mm; Body_With_Dia=290 mm; Body_With_Dia_1=363 mm; Body_With_Dia_2=392 mm; Bolt_support=1115 mm; Bolt_support_2=558 mm; Bolt_support_Dia=60 mm; Bolt_support_lenght=320 mm; Bolt_support_lenght_2=330 mm; Bottom_profile=150 mm; D1=360 mm; D3=420 mm; D3_Ref=890 mm; DN=600 mm; Fillet_Length=30 mm  [stored 0.0984252 ft]; Flange_thickness=36 mm  [stored 0.11811 ft]; H3=1345 mm; ID=300 mm; L=1450 mm; PG_Dia=200 mm; PG_Ref=242 mm; PG_depth=42 mm  [stored 0.137795 ft]; PG_height=870 mm; PG_height_1=770 mm; PG_ref=320 mm; PR_1=75 mm; P_lenght=175 mm; Pilot_Dia_1=106 mm; Pilot_Dia_2=159 mm; Pilot_Dia_3=71 mm; Pilot_Dia_4=35 mm  [stored 0.114829 ft]; Pilot_Dia_5=24 mm  [stored 0.0787402 ft]; Pilot_top_1=814 mm; Pilot_top_ref=101 mm; Profile1_Height=530 mm; Profile1_Length=114 mm; Profile1_Length_2=76 mm; Profile_Dia=30 mm  [stored 0.0984252 ft]; Profile_Dia_2=30 mm  [stored 0.0984252 ft]; Profile_Dia_3=60 mm; Profile_height ref=65 mm; T_Height=330 mm; T_Height_2=283 mm; T_Height_Ref_1=47 mm; T_Height_Ref_2=55 mm; Top_Profile=669 mm; Top_Profile_Ref=674 mm; W=1030 mm; W_Ref=811 mm; W_Ref_2=940 mm
- 879-0600-00-144000511A0_DN600_PN16: Body_Collar_Dia=151 mm; Body_Collar_Dia_2=130 mm; Body_Flange_Dia=414 mm; Body_Flange_Dia_2=453 mm; Body_Height_1=363 mm; Body_Height_2=181 mm; Body_Height_3=145 mm; Body_Height_4=196 mm; Body_Top_Dia=65 mm; Body_Top_Dia_2=54 mm; Body_With_Dia=290 mm; Body_With_Dia_1=363 mm; Body_With_Dia_2=392 mm; Bolt_support=1115 mm; Bolt_support_2=558 mm; Bolt_support_Dia=60 mm; Bolt_support_lenght=320 mm; Bolt_support_lenght_2=330 mm; Bottom_profile=150 mm; D1=360 mm; D3=420 mm; D3_Ref=890 mm; DN=600 mm; Fillet_Length=30 mm  [stored 0.0984252 ft]; Flange_thickness=36 mm  [stored 0.11811 ft]; H3=1518 mm; ID=300 mm; L=1450 mm; PG_Dia=200 mm; PG_Ref=242 mm; PG_depth=42 mm  [stored 0.137795 ft]; PG_height=913 mm; PG_height_1=813 mm; PG_ref=320 mm; PR_1=113 mm; P_lenght=175 mm; Pilot_Dia_1=106 mm; Pilot_Dia_2=159 mm; Pilot_Dia_3=71 mm; Pilot_Dia_4=35 mm  [stored 0.114829 ft]; Pilot_Dia_5=24 mm  [stored 0.0787402 ft]; Pilot_top_1=901 mm; Pilot_top_ref=187 mm; Profile1_Height=535 mm; Profile1_Length=114 mm; Profile1_Length_2=76 mm; Profile_Dia=30 mm  [stored 0.0984252 ft]; Profile_Dia_2=30 mm  [stored 0.0984252 ft]; Profile_Dia_3=60 mm; Profile_height ref=65 mm; T_Height=498 mm; T_Height_2=427 mm; T_Height_Ref_1=71 mm; T_Height_Ref_2=83 mm; Top_Profile=669 mm; Top_Profile_Ref=674 mm; W=1030 mm; W_Ref=811 mm; W_Ref_2=940 mm

note: [stored X ft] marks values corroborated as IEEE doubles in the binary element streams (Revit-internal decimal feet)

## geometry (parser evidence)
native form markers: Sweep x4
no freeform markers — native parametric forms only
